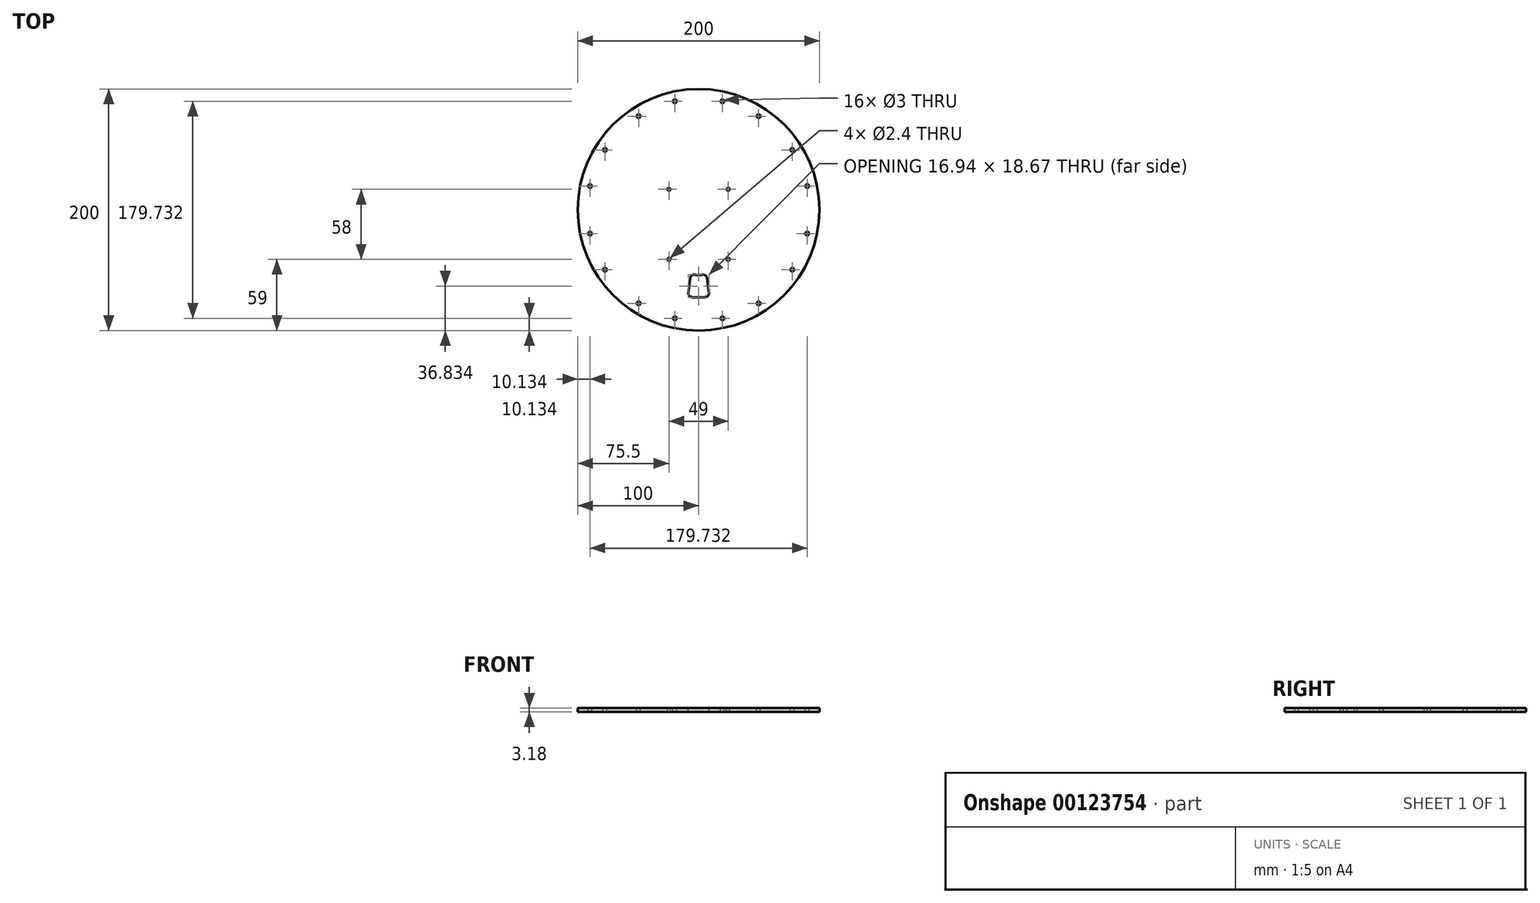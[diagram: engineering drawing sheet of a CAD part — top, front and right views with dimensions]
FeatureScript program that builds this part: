
annotation { "Feature Type Name" : "Feature", "Feature Type Description" : "" }
export const myFeature = defineFeature(function(context is Context, id is Id, definition is map)
    precondition{}
    {
        {
            var Q0;
            Q0=qCreatedBy(makeId("Top.planeOp"),FACE);
            var sketch = newSketch(context, id + "F0", { "sketchPlane" : qUnion([Q0])});
            skCircle(sketch, "E0", {"center": v(0, 0) * mm, "radius": 100 * mm});
            skSolve(sketch);
        }
        {
            var Q0;
            Q0 = qSketchRegion(id + "F0", true);
            extrude(context, id + "F1", {"entities" : qUnion([Q0]), "depth" : 3.17 * mm});
        }
        {
            var Q0;
            Q0=makeQuery(id+"F1.opExtrude","CAP_FACE",FACE,{"disambiguationData":[OSD([sQuery(id+"F0.wireOp",EDGE,"E0")])],"isStart":false});
            var sketch = newSketch(context, id + "F2", { "sketchPlane" : qUnion([Q0])});
            skCircle(sketch, "E1", {"center": v(0, 0) * mm, "radius": 92 * mm, "construction": true});
            skLineSegment(sketch, "E2", {"start": v(-19.7, -89.87) * mm, "end": v(19.7, -89.87) * mm, "construction": true});
            skCircle(sketch, "E3", {"center": v(19.7, -89.87) * mm, "radius": 1.5 * mm});
            skCircle(sketch, "E4", {"center": v(-19.7, -89.87) * mm, "radius": 1.5 * mm});
            skCircle(sketch, "E5.1.0", {"center": v(-49.61, -77.47) * mm, "radius": 1.5 * mm});
            skCircle(sketch, "E5.1.1", {"center": v(-77.47, -49.61) * mm, "radius": 1.5 * mm});
            skCircle(sketch, "E5.2.0", {"center": v(-89.87, -19.7) * mm, "radius": 1.5 * mm});
            skCircle(sketch, "E5.2.1", {"center": v(-89.87, 19.7) * mm, "radius": 1.5 * mm});
            skCircle(sketch, "E5.3.0", {"center": v(-77.47, 49.61) * mm, "radius": 1.5 * mm});
            skCircle(sketch, "E5.3.1", {"center": v(-49.61, 77.47) * mm, "radius": 1.5 * mm});
            skCircle(sketch, "E5.4.0", {"center": v(-19.7, 89.87) * mm, "radius": 1.5 * mm});
            skCircle(sketch, "E5.4.1", {"center": v(19.7, 89.87) * mm, "radius": 1.5 * mm});
            skCircle(sketch, "E5.5.0", {"center": v(49.61, 77.47) * mm, "radius": 1.5 * mm});
            skCircle(sketch, "E5.5.1", {"center": v(77.47, 49.61) * mm, "radius": 1.5 * mm});
            skCircle(sketch, "E5.6.0", {"center": v(89.87, 19.7) * mm, "radius": 1.5 * mm});
            skCircle(sketch, "E5.6.1", {"center": v(89.87, -19.7) * mm, "radius": 1.5 * mm});
            skCircle(sketch, "E5.7.0", {"center": v(77.47, -49.61) * mm, "radius": 1.5 * mm});
            skCircle(sketch, "E5.7.1", {"center": v(49.61, -77.47) * mm, "radius": 1.5 * mm});
            skLineSegment(sketch, "E5.anchor1", {"start": v(0, 0) * mm, "end": v(19.7, -89.87) * mm, "construction": true});
            skLineSegment(sketch, "E5.anchor2", {"start": v(0, 0) * mm, "end": v(77.47, -49.61) * mm, "construction": true});
            skSolve(sketch);
        }
        {
            var Q0;
            Q0 = qSketchRegion(id + "F2", true);
            extrude(context, id + "F3", {"entities" : qUnion([Q0]), "operationType" : NewBodyOperationType.REMOVE, "endBound" : BoundingType.THROUGH_ALL, "oppositeDirection" : true, "depth" : 25 * mm});
        }
        {
            var Q0;
            Q0=makeQuery(id+"F1.opExtrude","CAP_FACE",FACE,{"disambiguationData":[OSD([sQuery(id+"F0.wireOp",EDGE,"E0")])],"isStart":false});
            var sketch = newSketch(context, id + "F4", { "sketchPlane" : qUnion([Q0])});
            skLineSegment(sketch, "E6.bottom", {"start": v(-24.5, -41) * mm, "end": v(24.5, -41) * mm, "construction": true});
            skLineSegment(sketch, "E6.top", {"start": v(-24.5, 17) * mm, "end": v(24.5, 17) * mm, "construction": true});
            skLineSegment(sketch, "E6.left", {"start": v(-24.5, -41) * mm, "end": v(-24.5, 17) * mm, "construction": true});
            skLineSegment(sketch, "E6.right", {"start": v(24.5, -41) * mm, "end": v(24.5, 17) * mm, "construction": true});
            skCircle(sketch, "E7", {"center": v(24.5, 17) * mm, "radius": 1.2 * mm});
            skCircle(sketch, "E8", {"center": v(24.5, -41) * mm, "radius": 1.2 * mm});
            skCircle(sketch, "E9", {"center": v(-24.5, -41) * mm, "radius": 1.2 * mm});
            skCircle(sketch, "E10", {"center": v(-24.5, 17) * mm, "radius": 1.2 * mm});
            skLineSegment(sketch, "E11", {"start": v(-24.5, -12) * mm, "end": v(24.5, -12) * mm, "construction": true});
            skLineSegment(sketch, "E12", {"start": v(0, 0) * mm, "end": v(0, -12) * mm, "construction": true});
            skSolve(sketch);
        }
        {
            var Q0;
            Q0 = qSketchRegion(id + "F4", true);
            extrude(context, id + "F5", {"entities" : qUnion([Q0]), "operationType" : NewBodyOperationType.REMOVE, "endBound" : BoundingType.THROUGH_ALL, "oppositeDirection" : true, "depth" : 25 * mm});
        }
        {
            var Q0;
            Q0=makeQuery(id+"F1.opExtrude","CAP_FACE",FACE,{"disambiguationData":[OSD([sQuery(id+"F0.wireOp",EDGE,"E0")])],"isStart":false});
            var sketch = newSketch(context, id + "F6", { "sketchPlane" : qUnion([Q0])});
            skArc(sketch, "E13", {"start": v(-10.32, -71.76) * mm, "mid": v(-9.57, -71.86) * mm, "end": v(-8.83, -71.96) * mm, "construction": true});
            skLineSegment(sketch, "E14", {"start": v(10.32, -71.76) * mm, "end": v(30.12, -65.95) * mm, "construction": true});
            skLineSegment(sketch, "E15", {"start": v(30.12, -65.95) * mm, "end": v(47.48, -54.8) * mm, "construction": true});
            skLineSegment(sketch, "E16", {"start": v(47.48, -54.8) * mm, "end": v(61, -39.2) * mm, "construction": true});
            skLineSegment(sketch, "E17", {"start": v(61, -39.2) * mm, "end": v(69.56, -20.43) * mm, "construction": true});
            skLineSegment(sketch, "E18", {"start": v(69.56, -20.43) * mm, "end": v(72.5, 0) * mm, "construction": true});
            skArc(sketch, "E19", {"start": v(-7.68, -53.41) * mm, "mid": v(-7.13, -53.49) * mm, "end": v(-6.57, -53.56) * mm, "construction": true});
            skLineSegment(sketch, "E20", {"start": v(10.32, -71.76) * mm, "end": v(-10.32, -71.76) * mm, "construction": true});
            skLineSegment(sketch, "E21", {"start": v(7.68, -53.41) * mm, "end": v(10.32, -71.76) * mm, "construction": true});
            skPoint(sketch, "E22", {"position": v(7.68, -53.41) * mm});
            skLineSegment(sketch, "E23", {"start": v(-7.68, -53.41) * mm, "end": v(-10.32, -71.76) * mm, "construction": true});
            skArc(sketch, "E24.trimOffspring", {"start": v(69.56, -20.43) * mm, "mid": v(71.76, -10.32) * mm, "end": v(72.5, 0) * mm, "construction": true});
            skLineSegment(sketch, "E25", {"start": v(-8.46, -68.92) * mm, "end": v(-6.93, -56.46) * mm});
            skLineSegment(sketch, "E26", {"start": v(8.46, -68.92) * mm, "end": v(6.93, -56.46) * mm});
            skLineSegment(sketch, "E27", {"start": v(-8.83, -71.96) * mm, "end": v(8.83, -71.96) * mm, "construction": true});
            skArc(sketch, "E28", {"start": v(8.83, -71.96) * mm, "mid": v(9.57, -71.86) * mm, "end": v(10.32, -71.76) * mm, "construction": true});
            skArc(sketch, "E29", {"start": v(-5.72, -72.27) * mm, "mid": v(0, -72.5) * mm, "end": v(5.72, -72.27) * mm});
            skArc(sketch, "E30", {"start": v(-3.74, -53.83) * mm, "mid": v(0, -53.96) * mm, "end": v(3.74, -53.83) * mm});
            skArc(sketch, "E31", {"start": v(6.57, -53.56) * mm, "mid": v(7.13, -53.49) * mm, "end": v(7.68, -53.41) * mm, "construction": true});
            skPoint(sketch, "E32.visualSharp", {"position": v(-6.57, -53.56) * mm});
            skArc(sketch, "E32.filletArc", {"start": v(-3.74, -53.83) * mm, "mid": v(-5.86, -54.51) * mm, "end": v(-6.93, -56.46) * mm});
            skPoint(sketch, "E33.visualSharp", {"position": v(6.57, -53.56) * mm});
            skArc(sketch, "E33.filletArc", {"start": v(6.93, -56.46) * mm, "mid": v(5.86, -54.51) * mm, "end": v(3.74, -53.83) * mm});
            skPoint(sketch, "E34.visualSharp", {"position": v(8.83, -71.96) * mm});
            skArc(sketch, "E34.filletArc", {"start": v(5.72, -72.27) * mm, "mid": v(7.8, -71.18) * mm, "end": v(8.46, -68.92) * mm});
            skPoint(sketch, "E35.visualSharp", {"position": v(-8.83, -71.96) * mm});
            skArc(sketch, "E35.filletArc", {"start": v(-8.46, -68.92) * mm, "mid": v(-7.8, -71.18) * mm, "end": v(-5.72, -72.27) * mm});
            skSolve(sketch);
        }
        {
            var Q0;
            Q0 = qSketchRegion(id + "F6", true);
            extrude(context, id + "F7", {"entities" : qUnion([Q0]), "operationType" : NewBodyOperationType.REMOVE, "endBound" : BoundingType.THROUGH_ALL, "oppositeDirection" : true, "depth" : 25 * mm});
        }
        {
            var Q0;
            Q0=qCreatedBy(makeId("Right.planeOp"),FACE);
            var sketch = newSketch(context, id + "F8", { "sketchPlane" : qUnion([Q0])});
            skLineSegment(sketch, "E36", {"start": v(0, 0) * mm, "end": v(0, 65.54) * mm});
            skSolve(sketch);
        }
    });
